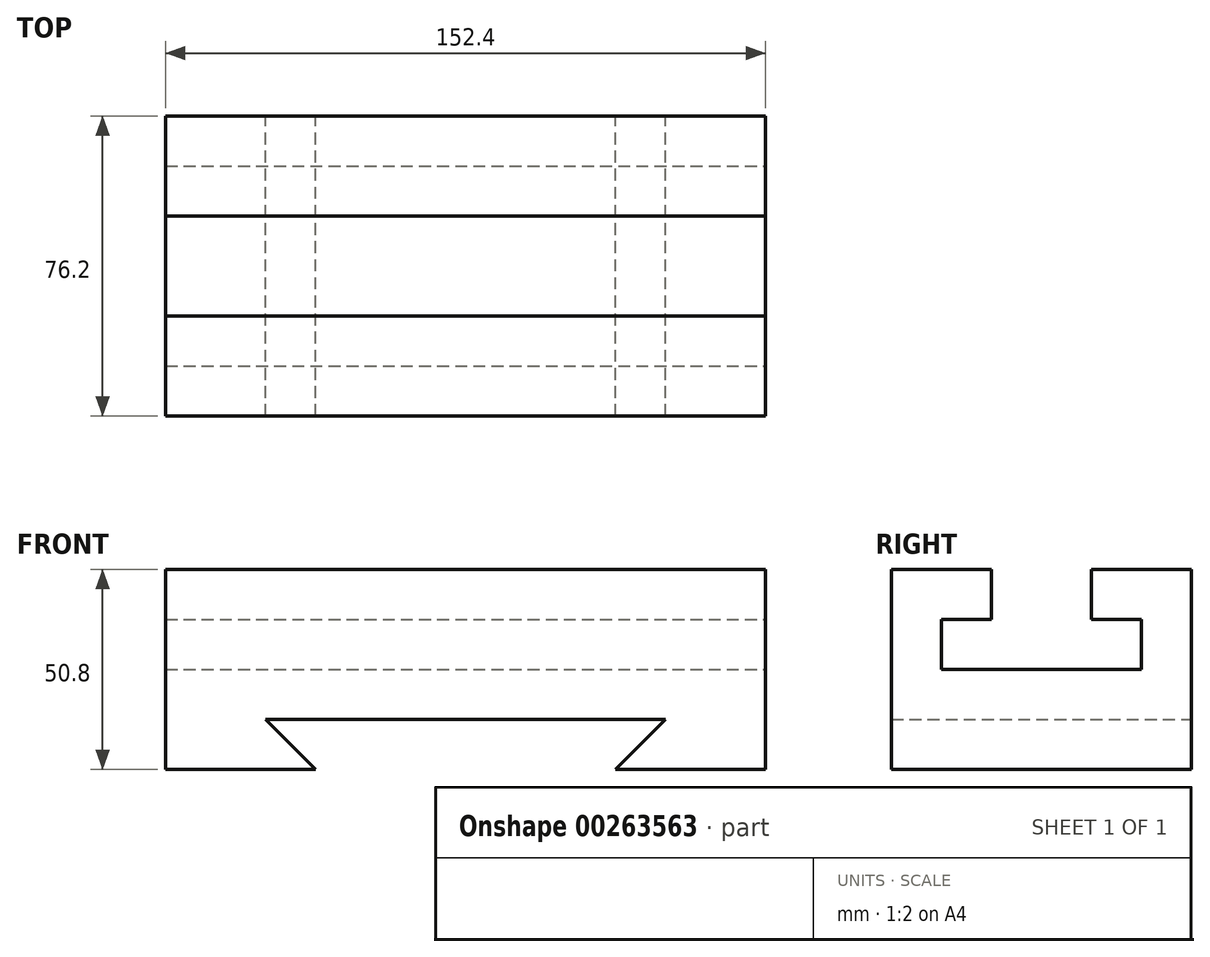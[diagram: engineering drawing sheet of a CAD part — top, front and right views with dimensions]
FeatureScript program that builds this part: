
annotation { "Feature Type Name" : "Feature", "Feature Type Description" : "" }
export const myFeature = defineFeature(function(context is Context, id is Id, definition is map)
    precondition{}
    {
        {
            var Q0;
            Q0=qCreatedBy(makeId("Front.planeOp"),FACE);
            var sketch = newSketch(context, id + "F0", { "sketchPlane" : qUnion([Q0])});
            skLineSegment(sketch, "E0", {"start": v(-75.98, 0) * mm, "end": v(-75.98, 12.7) * mm});
            skLineSegment(sketch, "E1", {"start": v(-50.58, 12.7) * mm, "end": v(51.02, 12.7) * mm});
            skLineSegment(sketch, "E2", {"start": v(76.42, 12.7) * mm, "end": v(76.42, 0) * mm});
            skLineSegment(sketch, "E3", {"start": v(76.42, 0) * mm, "end": v(38.32, 0) * mm});
            skLineSegment(sketch, "E4", {"start": v(51.02, 12.7) * mm, "end": v(38.32, 0) * mm});
            skLineSegment(sketch, "E5", {"start": v(-75.98, 0) * mm, "end": v(-37.88, 0) * mm});
            skLineSegment(sketch, "E6", {"start": v(-50.58, 12.7) * mm, "end": v(-37.88, 0) * mm});
            skLineSegment(sketch, "E7", {"start": v(-75.98, 0) * mm, "end": v(-75.98, 50.8) * mm});
            skLineSegment(sketch, "E8", {"start": v(-75.98, 50.8) * mm, "end": v(76.42, 50.8) * mm});
            skLineSegment(sketch, "E9", {"start": v(76.42, 50.8) * mm, "end": v(76.42, 0) * mm});
            skSolve(sketch);
        }
        {
            var Q0;
            Q0=makeQuery(id+"F0.imprint","IMPRINT",FACE,{"disambiguationData":[TD([[makeQuery(id+"F0.imprint","IMPRINT",EDGE,{"derivedFrom":sQuery(id+"F0.wireOp",EDGE,"E1")}),1.0]])]});
            extrude(context, id + "F1", {"entities" : qUnion([Q0]), "depth" : 76.2 * mm});
        }
        {
            var Q0;
            Q0=makeQuery(id+"F1.opExtrude","SWEPT_FACE",FACE,{"disambiguationData":[OSD([sQuery(id+"F0.wireOp",EDGE,"E9")])]});
            var sketch = newSketch(context, id + "F2", { "sketchPlane" : qUnion([Q0])});
            skLineSegment(sketch, "E10", {"start": v(0, 50.8) * mm, "end": v(-25.4, 50.8) * mm});
            skLineSegment(sketch, "E11", {"start": v(-25.4, 50.8) * mm, "end": v(-25.4, 38.1) * mm});
            skLineSegment(sketch, "E12", {"start": v(-25.4, 38.1) * mm, "end": v(-12.7, 38.1) * mm});
            skLineSegment(sketch, "E13", {"start": v(-12.7, 38.1) * mm, "end": v(-12.7, 25.4) * mm});
            skLineSegment(sketch, "E14", {"start": v(-12.7, 25.4) * mm, "end": v(-63.5, 25.4) * mm});
            skLineSegment(sketch, "E15", {"start": v(-63.5, 25.4) * mm, "end": v(-63.5, 38.1) * mm});
            skLineSegment(sketch, "E16", {"start": v(-63.5, 38.1) * mm, "end": v(-50.8, 38.1) * mm});
            skLineSegment(sketch, "E17", {"start": v(-50.8, 38.1) * mm, "end": v(-50.8, 50.8) * mm});
            skLineSegment(sketch, "E18", {"start": v(-50.8, 50.8) * mm, "end": v(-76.2, 50.8) * mm});
            skLineSegment(sketch, "E19", {"start": v(-50.8, 50.8) * mm, "end": v(-25.4, 50.8) * mm});
            skSolve(sketch);
        }
        {
            var Q0;
            Q0=makeQuery(id+"F2.imprint","IMPRINT",FACE,{"disambiguationData":[TD([[makeQuery(id+"F2.imprint","IMPRINT",EDGE,{"derivedFrom":sQuery(id+"F2.wireOp",EDGE,"E11")}),-1.0]])]});
            extrude(context, id + "F3", {"entities" : qUnion([Q0]), "operationType" : NewBodyOperationType.REMOVE, "oppositeDirection" : true, "depth" : 152.4 * mm});
        }
    });
